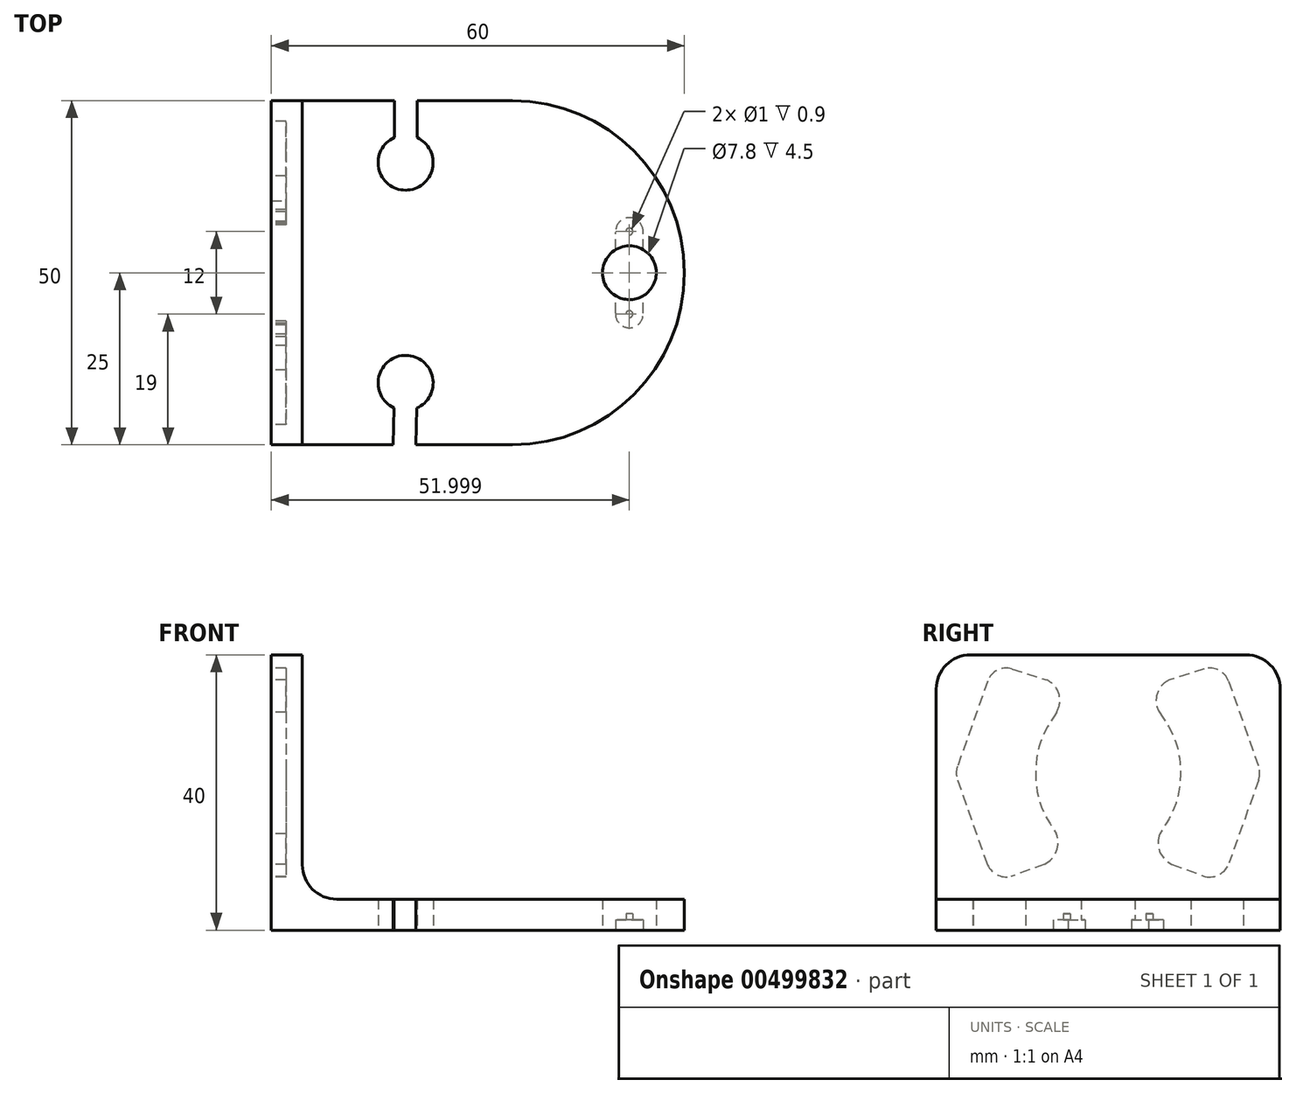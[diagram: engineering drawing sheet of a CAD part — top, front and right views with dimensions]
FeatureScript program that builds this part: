
annotation { "Feature Type Name" : "Feature", "Feature Type Description" : "" }
export const myFeature = defineFeature(function(context is Context, id is Id, definition is map)
    precondition{}
    {
        {
            var Q0;
            Q0=qCreatedBy(makeId("Front.planeOp"),FACE);
            var sketch = newSketch(context, id + "F0", { "sketchPlane" : qUnion([Q0])});
            skLineSegment(sketch, "E0", {"start": v(35.04, 0) * mm, "end": v(-24.96, 0) * mm});
            skLineSegment(sketch, "E1", {"start": v(-24.96, 0) * mm, "end": v(-24.96, 40) * mm});
            skLineSegment(sketch, "E2", {"start": v(-24.96, 40) * mm, "end": v(-20.46, 40) * mm});
            skLineSegment(sketch, "E3", {"start": v(-20.46, 40) * mm, "end": v(-20.46, 9.5) * mm});
            skLineSegment(sketch, "E4", {"start": v(-15.46, 4.5) * mm, "end": v(35.04, 4.5) * mm});
            skLineSegment(sketch, "E5", {"start": v(35.04, 4.5) * mm, "end": v(35.04, 0) * mm});
            skPoint(sketch, "E6.visualSharp", {"position": v(-20.46, 4.5) * mm});
            skArc(sketch, "E6.filletArc", {"start": v(-20.46, 9.5) * mm, "mid": v(-19, 5.96) * mm, "end": v(-15.46, 4.5) * mm});
            skSolve(sketch);
        }
        {
            var Q0;
            Q0 = qSketchRegion(id + "F0", true);
            extrude(context, id + "F1", {"entities" : qUnion([Q0]), "depth" : 50 * mm});
        }
        {
            var Q0;
            Q0=makeQuery(id+"F1.opExtrude","CAP_EDGE",EDGE,{"disambiguationData":[OSD([sQuery(id+"F0.wireOp",EDGE,"E5")])],"isStart":true});
            fillet(context, id + "F2", {"entities" : qUnion([Q0]), "radius" : 25 * mm, "tangentPropagation" : true, "allowEdgeOverflow" : false});
        }
        {
            var Q0;
            Q0=makeQuery(id+"F1.opExtrude","CAP_EDGE",EDGE,{"disambiguationData":[OSD([sQuery(id+"F0.wireOp",EDGE,"E5")])],"isStart":false});
            fillet(context, id + "F3", {"entities" : qUnion([Q0]), "radius" : 25 * mm, "tangentPropagation" : true, "allowEdgeOverflow" : false});
        }
        {
            var Q0;
            Q0=makeQuery(id+"F1.opExtrude","SWEPT_FACE",FACE,{"disambiguationData":[OSD([sQuery(id+"F0.wireOp",EDGE,"E4")])]});
            var sketch = newSketch(context, id + "F4", { "sketchPlane" : qUnion([Q0])});
            skCircle(sketch, "E7", {"center": v(27.04, -25) * mm, "radius": 3.9 * mm});
            skSolve(sketch);
        }
        {
            var Q0;
            Q0 = qSketchRegion(id + "F4", true);
            extrude(context, id + "F5", {"entities" : qUnion([Q0]), "operationType" : NewBodyOperationType.REMOVE, "endBound" : BoundingType.SYMMETRIC, "depth" : 25 * mm});
        }
        {
            var Q0;
            Q0=qCreatedBy(makeId("Top.planeOp"),FACE);
            var sketch = newSketch(context, id + "F6", { "sketchPlane" : qUnion([Q0])});
            skCircle(sketch, "E8", {"center": v(27.04, -31) * mm, "radius": 0.5 * mm});
            skSolve(sketch);
        }
        {
            var Q0;
            Q0=qCreatedBy(makeId("Top.planeOp"),FACE);
            var sketch = newSketch(context, id + "F7", { "sketchPlane" : qUnion([Q0])});
            skCircle(sketch, "E9", {"center": v(27.04, -19) * mm, "radius": 0.5 * mm});
            skSolve(sketch);
        }
        {
            var Q0;
            Q0 = qSketchRegion(id + "F7", true);
            extrude(context, id + "F8", {"entities" : qUnion([Q0]), "operationType" : NewBodyOperationType.REMOVE, "endBound" : BoundingType.SYMMETRIC, "depth" : 4.8 * mm});
        }
        {
            var Q0;
            Q0 = qSketchRegion(id + "F6", true);
            extrude(context, id + "F9", {"entities" : qUnion([Q0]), "operationType" : NewBodyOperationType.REMOVE, "endBound" : BoundingType.SYMMETRIC, "depth" : 4.8 * mm});
        }
        {
            var Q0;
            Q0=qCreatedBy(makeId("Top.planeOp"),FACE);
            var sketch = newSketch(context, id + "F10", { "sketchPlane" : qUnion([Q0])});
            skArc(sketch, "E10", {"start": v(25.04, -30.86) * mm, "mid": v(27.04, -33) * mm, "end": v(29.03, -30.86) * mm});
            skPoint(sketch, "E10.first.point", {"position": v(25.04, -30.86) * mm});
            skPoint(sketch, "E10.second.point", {"position": v(28.23, -32.6) * mm});
            skPoint(sketch, "E10.third.point", {"position": v(28.37, -29.51) * mm});
            skArc(sketch, "E11", {"start": v(29.03, -19.13) * mm, "mid": v(27, -17) * mm, "end": v(25.05, -19.2) * mm});
            skPoint(sketch, "E11.first.point", {"position": v(25.05, -19.2) * mm});
            skPoint(sketch, "E11.second.point", {"position": v(28.34, -20.52) * mm});
            skPoint(sketch, "E11.third.point", {"position": v(28.22, -17.39) * mm});
            skLineSegment(sketch, "E12.bottom", {"start": v(29.03, -30.86) * mm, "end": v(29.03, -30.86) * mm});
            skLineSegment(sketch, "E12.left", {"start": v(25.04, -30.86) * mm, "end": v(25.04, -19.13) * mm});
            skLineSegment(sketch, "E12.right", {"start": v(29.03, -30.86) * mm, "end": v(29.03, -19.13) * mm});
            skSolve(sketch);
        }
        {
            var Q0;
            Q0 = qSketchRegion(id + "F10", true);
            extrude(context, id + "F11", {"entities" : qUnion([Q0]), "operationType" : NewBodyOperationType.REMOVE, "depth" : 1.5 * mm});
        }
        {
            var Q0;
            Q0=makeQuery(id+"F1.opExtrude","CAP_EDGE",EDGE,{"disambiguationData":[OSD([sQuery(id+"F0.wireOp",EDGE,"E2")])],"isStart":false});
            fillet(context, id + "F12", {"entities" : qUnion([Q0]), "radius" : 5 * mm, "tangentPropagation" : true, "allowEdgeOverflow" : false});
        }
        {
            var Q0;
            Q0=makeQuery(id+"F1.opExtrude","CAP_EDGE",EDGE,{"disambiguationData":[OSD([sQuery(id+"F0.wireOp",EDGE,"E2")])],"isStart":true});
            fillet(context, id + "F13", {"entities" : qUnion([Q0]), "radius" : 5 * mm, "tangentPropagation" : true, "allowEdgeOverflow" : false});
        }
        {
            var Q0;
            Q0=makeQuery(id+"F1.opExtrude","SWEPT_FACE",FACE,{"disambiguationData":[OSD([sQuery(id+"F0.wireOp",EDGE,"E1")])]});
            var sketch = newSketch(context, id + "F14", { "sketchPlane" : qUnion([Q0])});
            skLineSegment(sketch, "E13", {"start": v(42.52, 36.18) * mm, "end": v(46.9, 23.81) * mm});
            skLineSegment(sketch, "E14", {"start": v(46.9, 21.8) * mm, "end": v(42.62, 9.72) * mm});
            skLineSegment(sketch, "E15", {"start": v(39, 37.93) * mm, "end": v(33.94, 36.36) * mm});
            skLineSegment(sketch, "E16", {"start": v(27.86, 29.27) * mm, "end": v(27.87, 29.1) * mm});
            skPoint(sketch, "E17.visualSharp", {"position": v(42.48, 24.1) * mm});
            skArc(sketch, "E17.filletArc", {"start": v(39.13, 7.8) * mm, "mid": v(41.24, 8.1) * mm, "end": v(42.62, 9.72) * mm});
            skArc(sketch, "E18.filletArc", {"start": v(46.9, 21.8) * mm, "mid": v(47.07, 22.8) * mm, "end": v(46.9, 23.81) * mm});
            skPoint(sketch, "E19.visualSharp", {"position": v(41.6, 38.74) * mm});
            skArc(sketch, "E19.filletArc", {"start": v(42.52, 36.18) * mm, "mid": v(41.12, 37.76) * mm, "end": v(39, 37.93) * mm});
            skArc(sketch, "E20", {"start": v(33.94, 36.36) * mm, "mid": v(32.17, 34.34) * mm, "end": v(32.5, 31.68) * mm});
            skArc(sketch, "E21", {"start": v(32.56, 14.03) * mm, "mid": v(32.53, 11.46) * mm, "end": v(34.28, 9.57) * mm});
            skLineSegment(sketch, "E22.trimOffspring", {"start": v(34.28, 9.57) * mm, "end": v(39.13, 7.8) * mm});
            skFitSpline(sketch, "E23", {"points": [v(32.5, 31.68) * mm, v(34.78, 27.56) * mm, v(35.53, 23.1) * mm, v(34.87, 18.36) * mm, v(32.56, 14.03) * mm], "startDerivative": vector(10.52, -16.1) * mm, "endDerivative": vector(-10.51, -16.47) * mm});
            skArc(sketch, "E24.MirrorCS", {"start": v(3.17, 21.8) * mm, "mid": v(3, 22.8) * mm, "end": v(3.17, 23.81) * mm});
            skLineSegment(sketch, "E25.MirrorCS", {"start": v(18.75, 29.27) * mm, "end": v(18.75, 29.1) * mm});
            skArc(sketch, "E26.MirrorCS", {"start": v(7.55, 36.18) * mm, "mid": v(8.95, 37.76) * mm, "end": v(11.06, 37.93) * mm});
            skLineSegment(sketch, "E27.MirrorCS", {"start": v(3.17, 21.8) * mm, "end": v(7.45, 9.72) * mm});
            skLineSegment(sketch, "E28.MirrorCS", {"start": v(7.55, 36.18) * mm, "end": v(3.17, 23.81) * mm});
            skPoint(sketch, "E29.MirrorP", {"position": v(8.46, 38.74) * mm});
            skPoint(sketch, "E30.MirrorP", {"position": v(7.6, 24.1) * mm});
            skArc(sketch, "E31.MirrorCS", {"start": v(16.13, 36.36) * mm, "mid": v(17.9, 34.34) * mm, "end": v(17.57, 31.68) * mm});
            skLineSegment(sketch, "E32.MirrorCS", {"start": v(11.06, 37.93) * mm, "end": v(16.13, 36.36) * mm});
            skLineSegment(sketch, "E33.MirrorCS", {"start": v(15.79, 9.57) * mm, "end": v(10.93, 7.8) * mm});
            skArc(sketch, "E34.MirrorCS", {"start": v(10.93, 7.8) * mm, "mid": v(8.83, 8.1) * mm, "end": v(7.45, 9.72) * mm});
            skFitSpline(sketch, "E35.MirrorCS", {"points": [v(17.57, 31.68) * mm, v(15.29, 27.56) * mm, v(14.53, 23.1) * mm, v(15.2, 18.36) * mm, v(17.51, 14.03) * mm], "startDerivative": vector(-10.52, -16.1) * mm, "endDerivative": vector(10.51, -16.47) * mm});
            skArc(sketch, "E36.MirrorCS", {"start": v(17.51, 14.03) * mm, "mid": v(17.53, 11.46) * mm, "end": v(15.79, 9.57) * mm});
            skSolve(sketch);
        }
        {
            var Q0;
            Q0 = qSketchRegion(id + "F14", true);
            extrude(context, id + "F15", {"entities" : qUnion([Q0]), "operationType" : NewBodyOperationType.REMOVE, "oppositeDirection" : true, "depth" : 2.1 * mm});
        }
        {
            var Q0;
            Q0=qCreatedBy(makeId("Top.planeOp"),FACE);
            var sketch = newSketch(context, id + "F16", { "sketchPlane" : qUnion([Q0])});
            skArc(sketch, "E37", {"start": v(-7.1, -5.35) * mm, "mid": v(-5.46, -13) * mm, "end": v(-3.8, -5.36) * mm});
            skArc(sketch, "E38", {"start": v(-3.87, -44.67) * mm, "mid": v(-5.4, -37) * mm, "end": v(-7.17, -44.62) * mm});
            skLineSegment(sketch, "E39.bottom", {"start": v(-3.8, 0) * mm, "end": v(-7.1, 0) * mm});
            skLineSegment(sketch, "E39.left", {"start": v(-3.8, 0) * mm, "end": v(-3.8, -5.36) * mm});
            skLineSegment(sketch, "E39.right", {"start": v(-7.1, 0) * mm, "end": v(-7.1, -5.35) * mm});
            skPoint(sketch, "E39.top.end.orphan", {"position": v(-7.12, -18) * mm});
            skPoint(sketch, "E39.top.start.orphan", {"position": v(-3.82, -18) * mm});
            skLineSegment(sketch, "E40.bottom", {"start": v(-3.95, -50) * mm, "end": v(-7.25, -50) * mm});
            skLineSegment(sketch, "E40.left", {"start": v(-3.95, -50) * mm, "end": v(-3.87, -44.67) * mm});
            skLineSegment(sketch, "E40.right", {"start": v(-7.25, -50) * mm, "end": v(-7.17, -44.62) * mm});
            skPoint(sketch, "E41.orphan", {"position": v(-6.98, -32) * mm});
            skPoint(sketch, "E42.orphan", {"position": v(-3.68, -32) * mm});
            skSolve(sketch);
        }
        {
            var Q0;
            Q0 = qSketchRegion(id + "F16", true);
            extrude(context, id + "F17", {"entities" : qUnion([Q0]), "operationType" : NewBodyOperationType.REMOVE, "depth" : 25 * mm});
        }
        {
            var Q0;
            Q0 = qSketchRegion(id + "F16", true);
            extrude(context, id + "F18", {"entities" : qUnion([Q0]), "operationType" : NewBodyOperationType.REMOVE, "depth" : 25 * mm});
        }
    });
